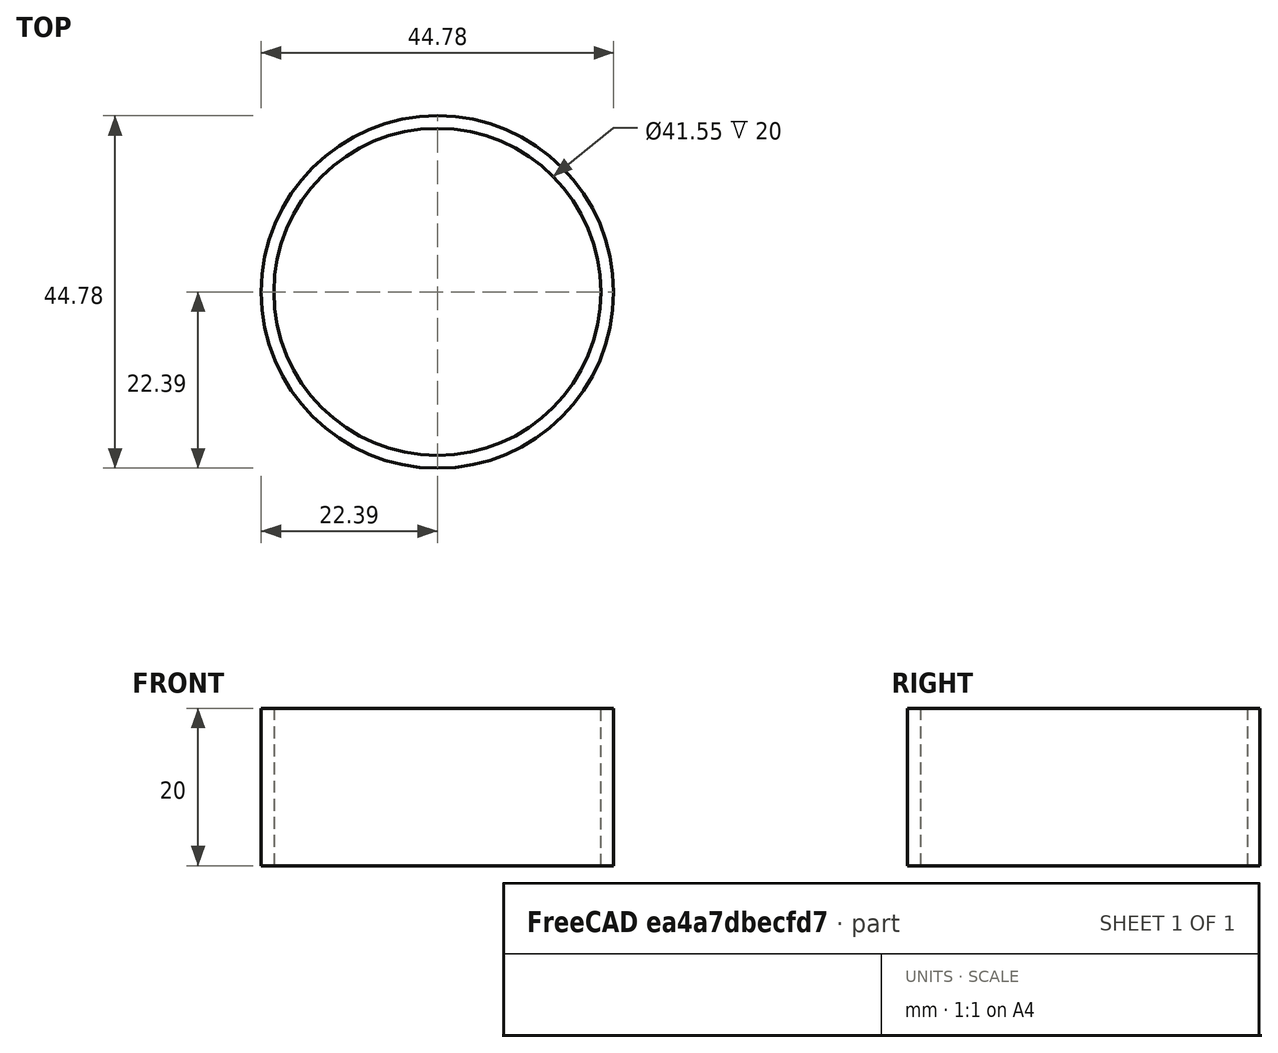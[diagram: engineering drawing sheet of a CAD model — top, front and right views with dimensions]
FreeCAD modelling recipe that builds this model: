
FCSTD DOCUMENT  (FreeCAD 1.1R20260325 (Git shallow))
Label: Measures001
License: All rights reserved
LicenseURL: https://en.wikipedia.org/wiki/All_rights_reserved
objects: TechDraw::DrawProjGroupItem×2, TechDraw::DrawViewDimension×2, App::Point×1, Sketcher::SketchObject×1, PartDesign::Pad×1, PartDesign::Body×1, TechDraw::DrawSVGTemplate×1, TechDraw::DrawProjGroup×1, TechDraw::DrawViewImage×1, TechDraw::DrawPage×1
note: 10 computed .brp shape members not serialized (recipe doc carries the construction recipe); baked Part::Feature solids carry a one-line shape summary decoded from their .brp

FEATURE [App::Point] Origin001
  Role = Origin
FEATURE [Sketcher::SketchObject] Sketch
  ArcFitTolerance = 1e-06
  AttachmentSupport = -> [Origin]
  ExternalTypes = [0]
  FullyConstrained = true
  MakeInternals = false
  MapMode = 5
  _ExternalGeoVersion = 1
  sketch-geometry (2):
    g0: Circle CenterX=0 CenterY=0 CenterZ=0 NormalX=0 NormalY=0 NormalZ=1 AngleXU=0 Radius=22.385
    g1: Circle CenterX=0 CenterY=0 CenterZ=0 NormalX=0 NormalY=0 NormalZ=1 AngleXU=0 Radius=20.775
  constraints (4):
    c: Diameter(g0) = 44.77
    c: Coincident(g0,g-1)
    c: Diameter(g1) = 41.55
    c: Coincident(g1,g0)
FEATURE [PartDesign::Pad] Pad
  Direction = (0,0,1)
  Length = 20
  Length2 = 10
  Profile = -> Sketch
  ReferenceAxis = -> Sketch [N_Axis]
  Refine = true
  SideType = 0
  Suppressed = false
  Type = 0
  Type2 = 0
FEATURE [PartDesign::Body] Body
  AllowCompound = true
  Group = -> [Sketch,Pad]
  Origin = -> Origin
  Tip = -> Pad
FEATURE [TechDraw::DrawSVGTemplate] Template
  Height = 210
  Orientation = 1
  Template = C:/Program Files/FreeCAD 1.1/data/Mod/TechDraw/Templates/Default_Template_A4_Landscape.svg
  Width = 297
FEATURE [TechDraw::DrawProjGroupItem] View  label="Front"
  CoarseView = false
  Direction = (0,-1,0)
  Focus = 100
  HardHidden = false
  IsoCount = 0
  IsoHidden = false
  IsoVisible = false
  LockPosition = true
  Perspective = false
  Rotation = 0
  RotationVector = (1,0,0)
  ScaleType = 2
  ScrubCount = 1
  SeamHidden = false
  SeamVisible = false
  SmoothHidden = false
  SmoothVisible = true
  Source = -> [Pad]
  Type = 0
  X = 0
  XDirection = (1,0,0)
  Y = 0
FEATURE [TechDraw::DrawProjGroupItem] ProjItem  label="FrontBottomRight"
  CoarseView = false
  Direction = (0.57735,-0.57735,-0.57735)
  Focus = 100
  HardHidden = false
  IsoCount = 0
  IsoHidden = false
  IsoVisible = false
  LockPosition = false
  Perspective = false
  Rotation = 0
  RotationVector = (1,0,0)
  ScaleType = 0
  ScrubCount = 1
  SeamHidden = false
  SeamVisible = false
  SmoothHidden = false
  SmoothVisible = true
  Source = -> [Pad]
  Type = 9
  X = -59.77
  XDirection = (0.707107,0.707107,0)
  Y = 46.089
FEATURE [TechDraw::DrawProjGroup] ProjGroup
  Anchor = -> View
  AutoDistribute = true
  LockPosition = false
  ProjectionType = 0
  Rotation = 0
  ScaleType = 0
  Source = -> [Pad]
  Views = -> [View,ProjItem]
  X = 148.5
  Y = 105
  spacingX = 15
  spacingY = 15
FEATURE [TechDraw::DrawViewImage] ActiveView
  Height = 102.4
  ImageFile = <userpath>/AppData/Local/Temp//FreeCAD/Cache/FreeCAD_Doc_a7555e05-4bd1-470a-a767-a1aa7ec02fc4_b49750_899293/Pag5950.tmp.png
  LockPosition = false
  Rotation = 0
  ScaleType = 2
  Width = 128
  X = 61.4269
  Y = 100.129
FEATURE [TechDraw::DrawViewDimension] Dimension
  AngleOverride = false
  Arbitrary = false
  ArbitraryTolerances = false
  BoxCorners = (2) [(-22.385,-10,-1e-07),(22.385,10,1e-07)]
  EqualTolerance = true
  ExtensionAngle = 0
  FormatSpec = %.2w
  FormatSpecOverTolerance = %+.2w
  FormatSpecUnderTolerance = %+.2w
  Inverted = false
  LineAngle = 0
  LockPosition = false
  MeasureType = 1
  OverTolerance = 0
  References2D = -> [View]
  Rotation = 0
  ScaleType = 0
  ShowUnits = false
  TheoreticalExact = false
  Type = 2
  UnderTolerance = 0
  UseActualArea = true
  X = 35.4381
  Y = 0
FEATURE [TechDraw::DrawViewDimension] Dimension001
  AngleOverride = false
  Arbitrary = false
  ArbitraryTolerances = false
  BoxCorners = (2) [(-22.385,-10,-1e-07),(22.385,10,1e-07)]
  EqualTolerance = true
  ExtensionAngle = 0
  FormatSpec = %.2w
  FormatSpecOverTolerance = %+.2w
  FormatSpecUnderTolerance = %+.2w
  Inverted = false
  LineAngle = 0
  LockPosition = false
  MeasureType = 1
  OverTolerance = 0
  References2D = -> [View]
  Rotation = 0
  ScaleType = 0
  ShowUnits = false
  TheoreticalExact = false
  Type = 1
  UnderTolerance = 0
  UseActualArea = true
  X = -4.81178
  Y = 22.9706
FEATURE [TechDraw::DrawPage] Page
  KeepUpdated = true
  NextBalloonIndex = 1
  ProjectionType = 0
  Template = -> Template
  Views = -> [ProjGroup,ActiveView,Dimension,Dimension001]
